# Revit family: kawneer-2000t-sgl_20607
name_source: partatom
category: Doors
revit_build: Autodesk Revit 2015 (Build: 20140905_0730(x64)
units: mm (PartAtom-declared; Revit-internal decimal feet)

## types (1)
- kawneer-2000t-sgl_20607
    2-Color Option = yes
    Air Infiltration (ASTM E 283) = < 0.30 cfm/ft2  @ 6.24 psf (300 Pa), Single Doors
    Application = exterior balconies
    Assembly Code = B2030110
    CSI Masterformat Code = 08 41 13
    Color = any
    Depth = 4"
    Description = The "2000T Terrace Door" is a thermally broken high performance French style door for use in condominiums, lofts, hotels and apartments.  It features mitered corner construction with heavy duty corner clips, stainless steel locking hardware and designed to meet the code requirements of windborne debris protection.
    Design Load = 60 psf (2873 Pa)
    Design Pressure = 40 psf (1915 Pa)
    Door Corner Construction = Mitered, heavy duty internal corner clip
    Door Handle Material = Aluminum - ASTM B 221 - 6063-T6 alloy and temper
    Door Handle Width = 28 7/8"
    Door Hangle Height = 33 1/8"
    Door Panel Material = Aluminum - ASTM B 221 - 6063-T6 alloy and temper
    Function = Interior
    Function (Interior or Exterior) = Exterior
    Glass Capture = Captured
    Glass Installtion = outside
    Glass U-Factor = 0.48
    Height = 84"
    Hinging Types = Butt Hinge
    Hurricane Resistant Tested = Small missile
Large missile
    Keywords = Entrance, Door, Swing Door, French Door, Balcony Door, Thermally Broken Door
    Manufacturer = Kawneer
    Manufacturer Part Number = 2000T Terrace Door
    Model = 2000T Terrace Door
    Overall U-Factor = 0.5646
    Panel Inserts Material = Glass
    Product data url = https://bimobject.com
    Short Description = Narrow Stile Terrace Access Door
    Thermal Transmittance = <0.57 BTU/hr/ff/F
    Type Comments = Narrow Stile Terrace Access Door
    Type of Glazing = monolithic, insulating
    URL = http://www.kawneer.com
    Water - Static (ASTM E 331) = In-swing - 6.24 psf (300 Pa)
Out-swing - 15.0 psf (718 Pa)
    Width = 32"

## geometry (parser evidence)
native form markers: Sweep x10
no freeform markers — native parametric forms only
